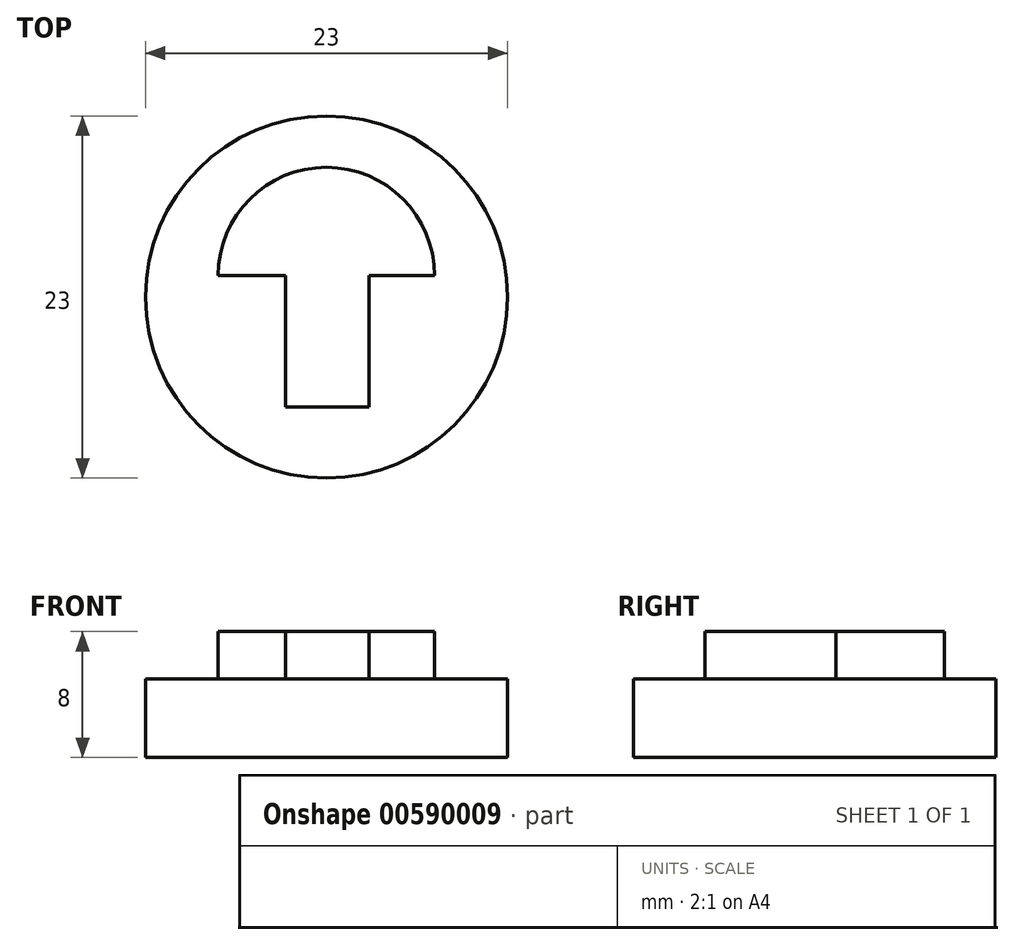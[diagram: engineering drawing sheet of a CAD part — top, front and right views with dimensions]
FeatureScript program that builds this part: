
annotation { "Feature Type Name" : "Feature", "Feature Type Description" : "" }
export const myFeature = defineFeature(function(context is Context, id is Id, definition is map)
    precondition{}
    {
        {
            var Q0;
            Q0=qCreatedBy(makeId("Top.planeOp"),FACE);
            var sketch = newSketch(context, id + "F0", { "sketchPlane" : qUnion([Q0])});
            skCircle(sketch, "E0", {"center": v(-36.43, 37.81) * mm, "radius": 11.5 * mm});
            skSolve(sketch);
        }
        {
            var Q0;
            Q0=makeQuery(id+"F0.imprint","IMPRINT",FACE,{"disambiguationData":[TD([[makeQuery(id+"F0.imprint","IMPRINT",EDGE,{"derivedFrom":sQuery(id+"F0.wireOp",EDGE,"E0")}),1.0]])]});
            extrude(context, id + "F1", {"entities" : qUnion([Q0]), "depth" : 5 * mm, "offsetDistance" : 25 * mm});
        }
        {
            var Q0;
            Q0=makeQuery(id+"F1.opExtrude","CAP_FACE",FACE,{"disambiguationData":[OSD([sQuery(id+"F0.wireOp",EDGE,"E0")])],"isStart":false});
            var sketch = newSketch(context, id + "F2", { "sketchPlane" : qUnion([Q0])});
            skArc(sketch, "E1", {"start": v(-29.57, 39.18) * mm, "mid": v(-36.44, 46.05) * mm, "end": v(-43.31, 39.18) * mm});
            skLineSegment(sketch, "E2", {"start": v(-29.57, 39.18) * mm, "end": v(-33.73, 39.18) * mm});
            skLineSegment(sketch, "E3.top", {"start": v(-39.04, 30.83) * mm, "end": v(-33.73, 30.83) * mm});
            skLineSegment(sketch, "E3.left", {"start": v(-39.04, 39.18) * mm, "end": v(-39.04, 30.83) * mm});
            skLineSegment(sketch, "E3.right", {"start": v(-33.73, 39.18) * mm, "end": v(-33.73, 30.83) * mm});
            skLineSegment(sketch, "E4.trimOffspring", {"start": v(-39.04, 39.18) * mm, "end": v(-43.31, 39.18) * mm});
            skSolve(sketch);
        }
        {
            var Q0;
            Q0=makeQuery(id+"F2.imprint","IMPRINT",FACE,{"disambiguationData":[TD([[makeQuery(id+"F2.imprint","IMPRINT",EDGE,{"derivedFrom":sQuery(id+"F2.wireOp",EDGE,"E1")}),1.0]])]});
            extrude(context, id + "F3", {"entities" : qUnion([Q0]), "operationType" : NewBodyOperationType.ADD, "depth" : 3 * mm, "offsetDistance" : 25 * mm});
        }
    });
